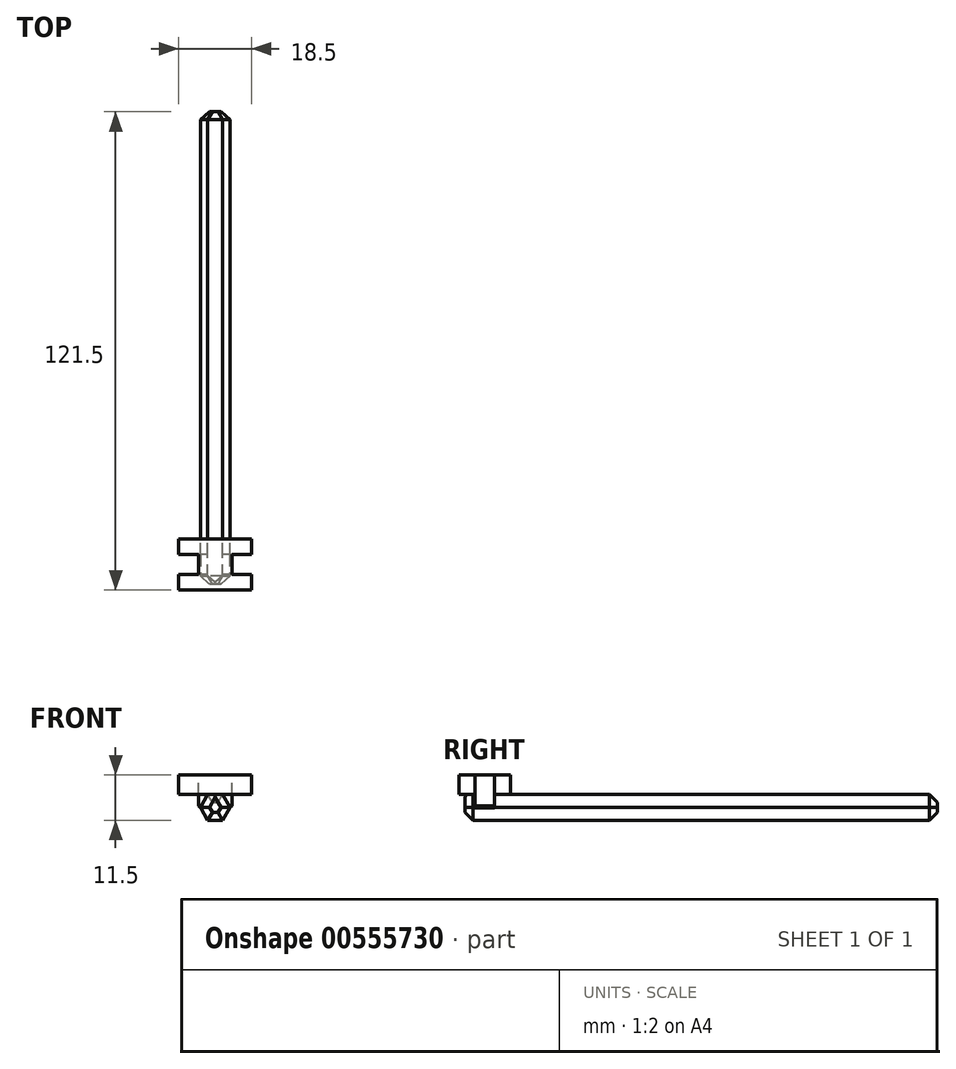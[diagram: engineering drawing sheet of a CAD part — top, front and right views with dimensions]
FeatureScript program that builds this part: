
annotation { "Feature Type Name" : "Feature", "Feature Type Description" : "" }
export const myFeature = defineFeature(function(context is Context, id is Id, definition is map)
    precondition{}
    {
        {
            var Q0;
            Q0=qCreatedBy(makeId("Front.planeOp"),FACE);
            var sketch = newSketch(context, id + "F0", { "sketchPlane" : qUnion([Q0])});
            skCircle(sketch, "E0.cCircle", {"center": v(0, 0) * mm, "radius": 3.25 * mm, "construction": true});
            skLineSegment(sketch, "E0.0", {"start": v(3.75, 0) * mm, "end": v(1.88, -3.25) * mm});
            skLineSegment(sketch, "E0.1", {"start": v(1.88, -3.25) * mm, "end": v(-1.88, -3.25) * mm});
            skLineSegment(sketch, "E0.2", {"start": v(-1.88, -3.25) * mm, "end": v(-3.75, 0) * mm});
            skLineSegment(sketch, "E0.3", {"start": v(-3.75, 0) * mm, "end": v(-1.88, 3.25) * mm});
            skLineSegment(sketch, "E0.4", {"start": v(-1.88, 3.25) * mm, "end": v(1.88, 3.25) * mm});
            skLineSegment(sketch, "E0.5", {"start": v(1.88, 3.25) * mm, "end": v(3.75, 0) * mm});
            skPoint(sketch, "E0.0.midPoint", {"position": v(2.81, -1.63) * mm});
            skSolve(sketch);
        }
        {
            var Q0;
            Q0=makeQuery(id+"F0.imprint","IMPRINT",FACE,{"disambiguationData":[TD([[makeQuery(id+"F0.imprint","IMPRINT",EDGE,{"derivedFrom":sQuery(id+"F0.wireOp",EDGE,"E0.0")}),-1.0]])]});
            extrude(context, id + "F1", {"entities" : qUnion([Q0]), "endBound" : BoundingType.SYMMETRIC, "depth" : 120 * mm, "offsetDistance" : 25 * mm});
        }
        {
            var Q0;
            Q0=makeQuery(id+"F1.opExtrude","SWEPT_FACE",FACE,{"disambiguationData":[OSD([sQuery(id+"F0.wireOp",EDGE,"E0.4")])]});
            var sketch = newSketch(context, id + "F2", { "sketchPlane" : qUnion([Q0])});
            skLineSegment(sketch, "E1.bottom", {"start": v(-4.25, -52.5) * mm, "end": v(4.25, -52.5) * mm});
            skLineSegment(sketch, "E1.top", {"start": v(-4.25, -57.5) * mm, "end": v(4.25, -57.5) * mm});
            skLineSegment(sketch, "E1.left", {"start": v(-4.25, -52.5) * mm, "end": v(-4.25, -57.5) * mm});
            skLineSegment(sketch, "E1.right", {"start": v(4.25, -52.5) * mm, "end": v(4.25, -57.5) * mm});
            skLineSegment(sketch, "E2.bottom", {"start": v(-4.25, 57.5) * mm, "end": v(4.25, 57.5) * mm});
            skLineSegment(sketch, "E2.top", {"start": v(-4.25, 52.5) * mm, "end": v(4.25, 52.5) * mm});
            skLineSegment(sketch, "E2.left", {"start": v(-4.25, 57.5) * mm, "end": v(-4.25, 52.5) * mm});
            skLineSegment(sketch, "E2.right", {"start": v(4.25, 57.5) * mm, "end": v(4.25, 52.5) * mm});
            skSolve(sketch);
        }
        {
            var Q0;
            {var subQ0=sQuery(id+"F2.wireOp",EDGE,"E1.left");Q0=makeQuery(id+"F2.imprint","IMPRINT",FACE,{"disambiguationData":[TD([[makeQuery(id+"F2.imprint","IMPRINT",EDGE,{"derivedFrom":subQ0}),1.0]])]});}
            var Q1;
            {var subQ0=sQuery(id+"F2.wireOp",EDGE,"E1.bottom");var subQ1=sQuery(id+"F0.wireOp",EDGE,"E0.4");var subQ2=makeQuery(id+"F1.opExtrude","SWEPT_EDGE",EDGE,{"disambiguationData":[OSD([sQuery(id+"F0.wireOp",EDGE,"E0.3"),subQ1])]});var subQ3=makeQuery(id+"F2.imprint","INTERSECT",VERTEX,{"derivedFrom":[subQ2,subQ0]});Q1=makeQuery(id+"F2.imprint","IMPRINT",FACE,{"disambiguationData":[TD([[makeQuery(id+"F2.imprint","IMPRINT",EDGE,{"disambiguationData":[TD([[subQ3,-1.0]])],"derivedFrom":subQ0}),-1.0]])]});}
            var Q2;
            {var subQ0=sQuery(id+"F2.wireOp",EDGE,"E1.right");Q2=makeQuery(id+"F2.imprint","IMPRINT",FACE,{"disambiguationData":[TD([[makeQuery(id+"F2.imprint","IMPRINT",EDGE,{"derivedFrom":subQ0}),-1.0]])]});}
            extrude(context, id + "F3", {"entities" : qUnion([Q0, Q1, Q2]), "operationType" : NewBodyOperationType.ADD, "endBound" : BoundingType.SYMMETRIC, "depth" : 10 * mm, "offsetDistance" : 25 * mm});
        }
        {
            var Q0;
            Q0=makeQuery(id+"F3.opExtrude","SWEPT_FACE",FACE,{"disambiguationData":[OSD([sQuery(id+"F2.wireOp",EDGE,"E1.top")])]});
            var sketch = newSketch(context, id + "F4", { "sketchPlane" : qUnion([Q0])});
            skLineSegment(sketch, "E3", {"start": v(-4.25, 3.25) * mm, "end": v(4.25, 3.25) * mm});
            skSolve(sketch);
        }
        {
            var Q0;
            {var subQ0=sQuery(id+"F4.wireOp",EDGE,"E3");Q0=makeQuery(id+"F4.imprint","IMPRINT",FACE,{"disambiguationData":[TD([[makeQuery(id+"F4.imprint","IMPRINT",EDGE,{"derivedFrom":subQ0}),1.0]])]});}
            extrude(context, id + "F5", {"entities" : qUnion([Q0]), "operationType" : NewBodyOperationType.ADD, "depth" : 4 * mm, "offsetDistance" : 25 * mm});
        }
        {
            var Q0;
            Q0=makeQuery(id+"F3.opExtrude","SWEPT_FACE",FACE,{"disambiguationData":[OSD([sQuery(id+"F2.wireOp",EDGE,"E1.bottom")])]});
            var sketch = newSketch(context, id + "F6", { "sketchPlane" : qUnion([Q0])});
            skLineSegment(sketch, "E4", {"start": v(-4.25, 3.25) * mm, "end": v(4.25, 3.25) * mm});
            skSolve(sketch);
        }
        {
            var Q0;
            {var subQ0=sQuery(id+"F6.wireOp",EDGE,"E4");Q0=makeQuery(id+"F6.imprint","IMPRINT",FACE,{"disambiguationData":[TD([[makeQuery(id+"F6.imprint","IMPRINT",EDGE,{"derivedFrom":subQ0}),1.0]])]});}
            extrude(context, id + "F7", {"entities" : qUnion([Q0]), "operationType" : NewBodyOperationType.ADD, "depth" : 4 * mm, "offsetDistance" : 25 * mm});
        }
        {
            var Q0;
            {var subQ0=sQuery(id+"F2.wireOp",EDGE,"E1.right");Q0=makeQuery(id+"F7.boolean.opBoolean","MERGE",FACE,{"derivedFrom":[makeQuery(id+"F5.boolean.opBoolean","MERGE",FACE,{"derivedFrom":[makeQuery(id+"F3.opExtrude","SWEPT_FACE",FACE,{"disambiguationData":[OSD([subQ0])]}),makeQuery(id+"F5.opExtrude","SWEPT_FACE",FACE,{"disambiguationData":[OSD([sQuery(id+"F2.wireOp",EDGE,"E1.top"),subQ0])]})]}),makeQuery(id+"F7.opExtrude","SWEPT_FACE",FACE,{"disambiguationData":[OSD([sQuery(id+"F2.wireOp",EDGE,"E1.bottom"),subQ0])]})]});}
            var sketch = newSketch(context, id + "F8", { "sketchPlane" : qUnion([Q0])});
            skLineSegment(sketch, "E5", {"start": v(-57.5, 3.25) * mm, "end": v(-57.5, 8.25) * mm});
            skLineSegment(sketch, "E6", {"start": v(-52.5, 3.25) * mm, "end": v(-52.5, 8.25) * mm});
            skSolve(sketch);
        }
        {
            var Q0;
            {var subQ0=sQuery(id+"F8.wireOp",EDGE,"E5");Q0=makeQuery(id+"F8.imprint","IMPRINT",FACE,{"disambiguationData":[TD([[makeQuery(id+"F8.imprint","IMPRINT",EDGE,{"derivedFrom":subQ0}),1.0]])]});}
            var Q1;
            {var subQ0=sQuery(id+"F8.wireOp",EDGE,"E6");Q1=makeQuery(id+"F8.imprint","IMPRINT",FACE,{"disambiguationData":[TD([[makeQuery(id+"F8.imprint","IMPRINT",EDGE,{"derivedFrom":subQ0}),-1.0]])]});}
            extrude(context, id + "F9", {"entities" : qUnion([Q0, Q1]), "operationType" : NewBodyOperationType.ADD, "depth" : 5 * mm, "offsetDistance" : 25 * mm});
        }
        {
            var Q0;
            {var subQ0=sQuery(id+"F2.wireOp",EDGE,"E1.left");Q0=makeQuery(id+"F7.boolean.opBoolean","MERGE",FACE,{"derivedFrom":[makeQuery(id+"F5.boolean.opBoolean","MERGE",FACE,{"derivedFrom":[makeQuery(id+"F3.opExtrude","SWEPT_FACE",FACE,{"disambiguationData":[OSD([subQ0])]}),makeQuery(id+"F5.opExtrude","SWEPT_FACE",FACE,{"disambiguationData":[OSD([sQuery(id+"F2.wireOp",EDGE,"E1.top"),subQ0])]})]}),makeQuery(id+"F7.opExtrude","SWEPT_FACE",FACE,{"disambiguationData":[OSD([sQuery(id+"F2.wireOp",EDGE,"E1.bottom"),subQ0])]})]});}
            var sketch = newSketch(context, id + "F10", { "sketchPlane" : qUnion([Q0])});
            skLineSegment(sketch, "E7", {"start": v(52.5, 3.25) * mm, "end": v(52.5, 8.25) * mm});
            skLineSegment(sketch, "E8", {"start": v(57.5, 3.25) * mm, "end": v(57.5, 8.25) * mm});
            skSolve(sketch);
        }
        {
            var Q0;
            {var subQ0=sQuery(id+"F10.wireOp",EDGE,"E7");Q0=makeQuery(id+"F10.imprint","IMPRINT",FACE,{"disambiguationData":[TD([[makeQuery(id+"F10.imprint","IMPRINT",EDGE,{"derivedFrom":subQ0}),1.0]])]});}
            var Q1;
            {var subQ0=sQuery(id+"F10.wireOp",EDGE,"E8");Q1=makeQuery(id+"F10.imprint","IMPRINT",FACE,{"disambiguationData":[TD([[makeQuery(id+"F10.imprint","IMPRINT",EDGE,{"derivedFrom":subQ0}),-1.0]])]});}
            extrude(context, id + "F11", {"entities" : qUnion([Q0, Q1]), "operationType" : NewBodyOperationType.ADD, "depth" : 5 * mm, "offsetDistance" : 25 * mm});
        }
        {
            var Q0;
            Q0=makeQuery(id+"F3.opExtrude","CAP_EDGE",EDGE,{"disambiguationData":[OSD([sQuery(id+"F2.wireOp",EDGE,"E1.right")])],"isStart":true});
            var Q1;
            Q1=makeQuery(id+"F3.opExtrude","CAP_EDGE",EDGE,{"disambiguationData":[OSD([sQuery(id+"F2.wireOp",EDGE,"E1.left")])],"isStart":true});
            chamfer(context, id + "F12", {"entities" : qUnion([Q0, Q1]), "width" : 2.2 * mm, "tangentPropagation" : true});
        }
        {
            var Q0;
            Q0=makeQuery(id+"F1.opExtrude","CAP_FACE",FACE,{"disambiguationData":[OSD([sQuery(id+"F0.wireOp",EDGE,"E0.0"),sQuery(id+"F0.wireOp",EDGE,"E0.1"),sQuery(id+"F0.wireOp",EDGE,"E0.2"),sQuery(id+"F0.wireOp",EDGE,"E0.3"),sQuery(id+"F0.wireOp",EDGE,"E0.4"),sQuery(id+"F0.wireOp",EDGE,"E0.5")])],"isStart":true});
            var Q1;
            Q1=makeQuery(id+"F1.opExtrude","CAP_EDGE",EDGE,{"disambiguationData":[OSD([sQuery(id+"F0.wireOp",EDGE,"E0.2")])],"isStart":false});
            var Q2;
            Q2=makeQuery(id+"F1.opExtrude","CAP_EDGE",EDGE,{"disambiguationData":[OSD([sQuery(id+"F0.wireOp",EDGE,"E0.1")])],"isStart":false});
            var Q3;
            Q3=makeQuery(id+"F1.opExtrude","CAP_EDGE",EDGE,{"disambiguationData":[OSD([sQuery(id+"F0.wireOp",EDGE,"E0.0")])],"isStart":false});
            var Q4;
            Q4=makeQuery(id+"F1.opExtrude","CAP_EDGE",EDGE,{"disambiguationData":[OSD([sQuery(id+"F0.wireOp",EDGE,"E0.5")])],"isStart":false});
            var Q5;
            Q5=makeQuery(id+"F1.opExtrude","CAP_EDGE",EDGE,{"disambiguationData":[OSD([sQuery(id+"F0.wireOp",EDGE,"E0.3")])],"isStart":false});
            chamfer(context, id + "F13", {"entities" : qUnion([Q0, Q1, Q2, Q3, Q4, Q5]), "width" : 2 * mm, "tangentPropagation" : true});
        }
    });
